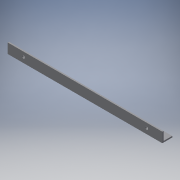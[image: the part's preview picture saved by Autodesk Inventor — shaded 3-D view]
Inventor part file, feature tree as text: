
AUTODESK INVENTOR PART (.ipt)
format: ipt  version: 2018 (Build 220112000, 112)  size: 116,224 bytes
history: native  units: mm
features: extrude x3, sketch x3
ambient origin geometry x8: Origin, YZ Plane, XZ Plane, XY Plane, X Axis, Y Axis, Z Axis, Center Point
bodies: Solid1 (feature_tree)
feature tree (6):
  extrude  "Extrusion1"  Depth=15.08mm
  extrude  "Extrusion2"  Depth=2.05mm
  extrude  "Extrusion3"  Depth=2.05mm
  sketch  "Sketch1"  dims[d0=234.5mm d1=15.08mm]
  sketch  "Sketch2"  dims[d2=2.05mm d3=0.0mm d4=2.05mm]
  sketch  "Sketch3"  dims[d5=13.03mm d6=0.0mm d7=93.5mm d8=93.5mm d9=8.0mm d10=8.0mm d11=2.05mm d12=0.0mm d13=4.2mm d14=4.2mm]
